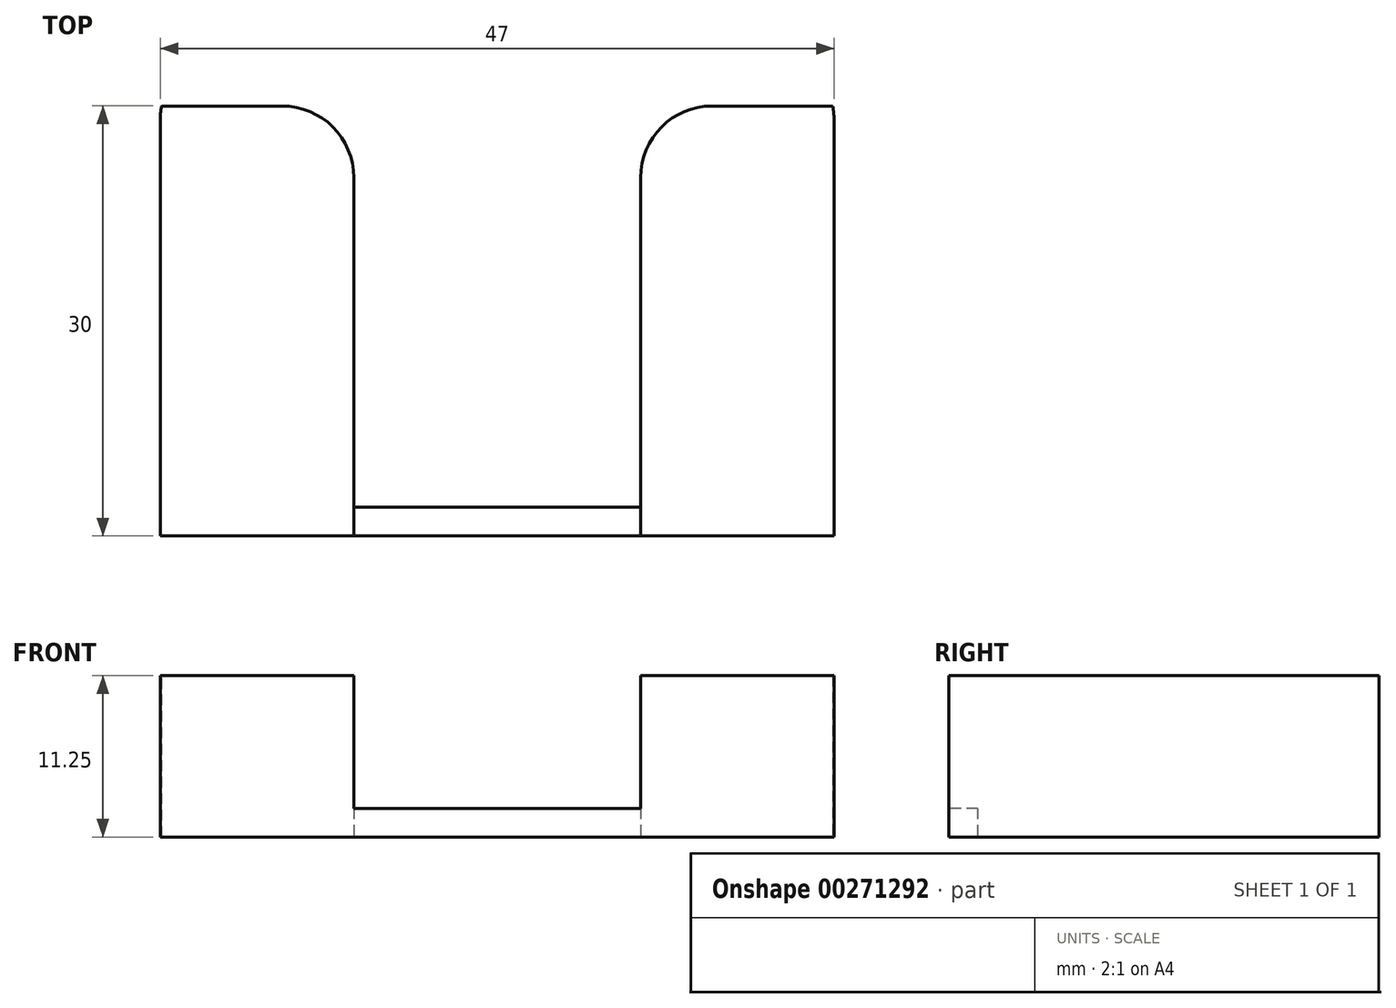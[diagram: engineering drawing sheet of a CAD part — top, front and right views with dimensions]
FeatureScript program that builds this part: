
annotation { "Feature Type Name" : "Feature", "Feature Type Description" : "" }
export const myFeature = defineFeature(function(context is Context, id is Id, definition is map)
    precondition{}
    {
        {
            var Q0;
            Q0=qCreatedBy(makeId("Top.planeOp"),FACE);
            var sketch = newSketch(context, id + "F0", { "sketchPlane" : qUnion([Q0])});
            skLineSegment(sketch, "E0.bottom", {"start": v(-22.69, 4.66) * mm, "end": v(24.31, 4.66) * mm});
            skLineSegment(sketch, "E0.top", {"start": v(-22.69, 0.66) * mm, "end": v(24.31, 0.66) * mm});
            skLineSegment(sketch, "E0.left", {"start": v(-22.69, 4.66) * mm, "end": v(-22.69, 0.66) * mm});
            skLineSegment(sketch, "E0.right", {"start": v(24.31, 4.66) * mm, "end": v(24.31, 0.66) * mm});
            skLineSegment(sketch, "E1.bottom", {"start": v(-22.69, 0.66) * mm, "end": v(-9.19, 0.66) * mm});
            skLineSegment(sketch, "E1.top", {"start": v(-22.69, -29.34) * mm, "end": v(-9.19, -29.34) * mm});
            skLineSegment(sketch, "E1.left", {"start": v(-22.69, 0.66) * mm, "end": v(-22.69, -29.34) * mm});
            skLineSegment(sketch, "E1.right", {"start": v(-9.19, 0.66) * mm, "end": v(-9.19, -29.34) * mm});
            skLineSegment(sketch, "E2.bottom", {"start": v(24.31, 0.66) * mm, "end": v(10.81, 0.66) * mm});
            skLineSegment(sketch, "E2.top", {"start": v(24.31, -29.34) * mm, "end": v(10.81, -29.34) * mm});
            skLineSegment(sketch, "E2.left", {"start": v(24.31, 0.66) * mm, "end": v(24.31, -29.34) * mm});
            skLineSegment(sketch, "E2.right", {"start": v(10.81, 0.66) * mm, "end": v(10.81, -29.34) * mm});
            skLineSegment(sketch, "E3.bottom", {"start": v(-5.64, -5.4) * mm, "end": v(7.26, -5.4) * mm});
            skLineSegment(sketch, "E3.top", {"start": v(-5.64, -25.3) * mm, "end": v(7.26, -25.3) * mm});
            skLineSegment(sketch, "E3.left", {"start": v(-5.64, -5.4) * mm, "end": v(-5.64, -25.3) * mm});
            skLineSegment(sketch, "E3.right", {"start": v(7.26, -5.4) * mm, "end": v(7.26, -25.3) * mm});
            skLineSegment(sketch, "E4.bottom", {"start": v(-9.19, -29.34) * mm, "end": v(10.81, -29.34) * mm});
            skLineSegment(sketch, "E4.top", {"start": v(-9.19, -27.34) * mm, "end": v(10.81, -27.34) * mm});
            skLineSegment(sketch, "E4.left", {"start": v(-9.19, -29.34) * mm, "end": v(-9.19, -27.34) * mm});
            skLineSegment(sketch, "E4.right", {"start": v(10.81, -29.34) * mm, "end": v(10.81, -27.34) * mm});
            skLineSegment(sketch, "E5.bottom", {"start": v(-7.69, 18.66) * mm, "end": v(7.31, 18.66) * mm});
            skLineSegment(sketch, "E5.top", {"start": v(-7.69, 4.66) * mm, "end": v(7.31, 4.66) * mm});
            skLineSegment(sketch, "E5.left", {"start": v(-7.69, 18.66) * mm, "end": v(-7.69, 4.66) * mm});
            skLineSegment(sketch, "E5.right", {"start": v(7.31, 18.66) * mm, "end": v(7.31, 4.66) * mm});
            skCircle(sketch, "E6", {"center": v(-0.19, 11.66) * mm, "radius": 3 * mm});
            skPoint(sketch, "E6.centerSnap0", {"position": v(-0.19, 18.66) * mm});
            skPoint(sketch, "E6.centerSnap1", {"position": v(-7.69, 11.66) * mm});
            skSolve(sketch);
        }
        {
            var Q0;
            Q0=makeQuery(id+"F0.imprint","IMPRINT",FACE,{"disambiguationData":[TD([[makeQuery(id+"F0.imprint","IMPRINT",EDGE,{"derivedFrom":sQuery(id+"F0.wireOp",EDGE,"E5.bottom")}),-1.0]])]});
            var Q1;
            Q1=makeQuery(id+"F0.imprint","IMPRINT",FACE,{"disambiguationData":[TD([[makeQuery(id+"F0.imprint","IMPRINT",EDGE,{"derivedFrom":sQuery(id+"F0.wireOp",EDGE,"E0.top")}),1.0]])]});
            var Q2;
            Q2=makeQuery(id+"F0.imprint","IMPRINT",FACE,{"disambiguationData":[TD([[makeQuery(id+"F0.imprint","IMPRINT",EDGE,{"derivedFrom":sQuery(id+"F0.wireOp",EDGE,"E1.bottom")}),-1.0]])]});
            var Q3;
            Q3=makeQuery(id+"F0.imprint","IMPRINT",FACE,{"disambiguationData":[TD([[makeQuery(id+"F0.imprint","IMPRINT",EDGE,{"derivedFrom":sQuery(id+"F0.wireOp",EDGE,"E2.bottom")}),1.0]])]});
            var Q4;
            Q4=makeQuery(id+"F0.imprint","IMPRINT",FACE,{"disambiguationData":[TD([[makeQuery(id+"F0.imprint","IMPRINT",EDGE,{"derivedFrom":sQuery(id+"F0.wireOp",EDGE,"E4.bottom")}),1.0]])]});
            extrude(context, id + "F1", {"entities" : qUnion([Q0, Q1, Q2, Q3, Q4]), "depth" : 2 * mm});
        }
        {
            var Q0;
            Q0=makeQuery(id+"F0.imprint","IMPRINT",FACE,{"disambiguationData":[TD([[makeQuery(id+"F0.imprint","IMPRINT",EDGE,{"derivedFrom":sQuery(id+"F0.wireOp",EDGE,"E0.top")}),-1.0]])]});
            extrude(context, id + "F2", {"entities" : qUnion([Q0]), "operationType" : NewBodyOperationType.ADD, "depth" : 11.25 * mm});
        }
        {
            var Q0;
            Q0=makeQuery(id+"F2.opExtrude","SWEPT_EDGE",EDGE,{"disambiguationData":[OSD([sQuery(id+"F0.wireOp",EDGE,"E0.top"),sQuery(id+"F0.wireOp",EDGE,"E2.bottom"),sQuery(id+"F0.wireOp",EDGE,"E2.right")])]});
            var Q1;
            Q1=makeQuery(id+"F2.opExtrude","SWEPT_EDGE",EDGE,{"disambiguationData":[OSD([sQuery(id+"F0.wireOp",EDGE,"E0.top"),sQuery(id+"F0.wireOp",EDGE,"E1.bottom"),sQuery(id+"F0.wireOp",EDGE,"E1.right")])]});
            var Q2;
            Q2=makeQuery(id+"F2.opExtrude","SWEPT_EDGE",EDGE,{"disambiguationData":[OSD([sQuery(id+"F0.wireOp",EDGE,"E1.right"),sQuery(id+"F0.wireOp",EDGE,"E4.top"),sQuery(id+"F0.wireOp",EDGE,"E4.left")])]});
            var Q3;
            Q3=makeQuery(id+"F2.opExtrude","SWEPT_EDGE",EDGE,{"disambiguationData":[OSD([sQuery(id+"F0.wireOp",EDGE,"E2.right"),sQuery(id+"F0.wireOp",EDGE,"E4.top"),sQuery(id+"F0.wireOp",EDGE,"E4.right")])]});
            var Q4;
            Q4=makeQuery(id+"F1.opExtrude","SWEPT_EDGE",EDGE,{"disambiguationData":[OSD([sQuery(id+"F0.wireOp",EDGE,"E2.top"),sQuery(id+"F0.wireOp",EDGE,"E2.left")])]});
            var Q5;
            Q5=makeQuery(id+"F1.opExtrude","SWEPT_EDGE",EDGE,{"disambiguationData":[OSD([sQuery(id+"F0.wireOp",EDGE,"E1.top"),sQuery(id+"F0.wireOp",EDGE,"E1.left")])]});
            var Q6;
            Q6=makeQuery(id+"F1.opExtrude","SWEPT_EDGE",EDGE,{"disambiguationData":[OSD([sQuery(id+"F0.wireOp",EDGE,"E0.bottom"),sQuery(id+"F0.wireOp",EDGE,"E0.right")])]});
            var Q7;
            Q7=makeQuery(id+"F1.opExtrude","SWEPT_EDGE",EDGE,{"disambiguationData":[OSD([sQuery(id+"F0.wireOp",EDGE,"E5.bottom"),sQuery(id+"F0.wireOp",EDGE,"E5.right")])]});
            var Q8;
            Q8=makeQuery(id+"F1.opExtrude","SWEPT_EDGE",EDGE,{"disambiguationData":[OSD([sQuery(id+"F0.wireOp",EDGE,"E5.bottom"),sQuery(id+"F0.wireOp",EDGE,"E5.left")])]});
            var Q9;
            Q9=makeQuery(id+"F1.opExtrude","SWEPT_EDGE",EDGE,{"disambiguationData":[OSD([sQuery(id+"F0.wireOp",EDGE,"E0.bottom"),sQuery(id+"F0.wireOp",EDGE,"E0.left")])]});
            var Q10;
            Q10=makeQuery(id+"F1.opExtrude","SWEPT_EDGE",EDGE,{"disambiguationData":[OSD([sQuery(id+"F0.wireOp",EDGE,"E0.bottom"),sQuery(id+"F0.wireOp",EDGE,"E5.top"),sQuery(id+"F0.wireOp",EDGE,"E5.left")])]});
            var Q11;
            Q11=makeQuery(id+"F1.opExtrude","SWEPT_EDGE",EDGE,{"disambiguationData":[OSD([sQuery(id+"F0.wireOp",EDGE,"E0.bottom"),sQuery(id+"F0.wireOp",EDGE,"E5.top"),sQuery(id+"F0.wireOp",EDGE,"E5.right")])]});
            fillet(context, id + "F3", {"entities" : qUnion([Q0, Q1, Q2, Q3, Q4, Q5, Q6, Q7, Q8, Q9, Q10, Q11]), "radius" : 5 * mm, "tangentPropagation" : true, "allowEdgeOverflow" : false});
        }
        {
            var Q0;
            {var subQ0=sQuery(id+"F0.wireOp",EDGE,"E4.top");var subQ1=sQuery(id+"F0.wireOp",EDGE,"E2.right");var subQ2=sQuery(id+"F0.wireOp",EDGE,"E1.right");var subQ3=sQuery(id+"F0.wireOp",EDGE,"E0.top");Q0=makeQuery(id+"F2.boolean.opBoolean","MERGE",FACE,{"derivedFrom":[makeQuery(id+"F1.opExtrude","CAP_FACE",FACE,{"disambiguationData":[OSD([sQuery(id+"F0.wireOp",EDGE,"E0.bottom"),subQ3,sQuery(id+"F0.wireOp",EDGE,"E0.left"),sQuery(id+"F0.wireOp",EDGE,"E0.right"),sQuery(id+"F0.wireOp",EDGE,"E1.top"),sQuery(id+"F0.wireOp",EDGE,"E1.left"),subQ2,sQuery(id+"F0.wireOp",EDGE,"E2.top"),sQuery(id+"F0.wireOp",EDGE,"E2.left"),subQ1,sQuery(id+"F0.wireOp",EDGE,"e83457b0-2eee-4cfc-8b23-16ca087f3800"),sQuery(id+"F0.wireOp",EDGE,"f83d8425-d4e3-404a-83f3-46c32a1b02bb"),sQuery(id+"F0.wireOp",EDGE,"E4.bottom"),subQ0,sQuery(id+"F0.wireOp",EDGE,"E5.bottom"),sQuery(id+"F0.wireOp",EDGE,"E5.left"),sQuery(id+"F0.wireOp",EDGE,"E5.right"),sQuery(id+"F0.wireOp",EDGE,"E6")])],"isStart":true}),makeQuery(id+"F2.opExtrude","CAP_FACE",FACE,{"disambiguationData":[OSD([subQ3,subQ2,subQ1,sQuery(id+"F0.wireOp",EDGE,"E3.bottom"),sQuery(id+"F0.wireOp",EDGE,"E3.top"),sQuery(id+"F0.wireOp",EDGE,"E3.left"),sQuery(id+"F0.wireOp",EDGE,"E3.right"),subQ0])],"isStart":true})]});}
            var sketch = newSketch(context, id + "F4", { "sketchPlane" : qUnion([Q0])});
            skLineSegment(sketch, "E7.bottom", {"start": v(-0.14, 25.3) * mm, "end": v(1.86, 25.3) * mm});
            skLineSegment(sketch, "E7.top", {"start": v(-0.14, 26.3) * mm, "end": v(1.86, 26.3) * mm});
            skLineSegment(sketch, "E7.left", {"start": v(-0.14, 25.3) * mm, "end": v(-0.14, 26.3) * mm});
            skLineSegment(sketch, "E7.right", {"start": v(1.86, 25.3) * mm, "end": v(1.86, 26.3) * mm});
            skLineSegment(sketch, "E8.bottom", {"start": v(-0.14, 5.4) * mm, "end": v(1.86, 5.4) * mm});
            skLineSegment(sketch, "E8.top", {"start": v(-0.14, 4.4) * mm, "end": v(1.86, 4.4) * mm});
            skLineSegment(sketch, "E8.left", {"start": v(-0.14, 5.4) * mm, "end": v(-0.14, 4.4) * mm});
            skLineSegment(sketch, "E8.right", {"start": v(1.86, 5.4) * mm, "end": v(1.86, 4.4) * mm});
            skSolve(sketch);
        }
        {
            var Q0;
            Q0=makeQuery(id+"F4.imprint","IMPRINT",FACE,{"disambiguationData":[TD([[makeQuery(id+"F4.imprint","IMPRINT",EDGE,{"derivedFrom":sQuery(id+"F4.wireOp",EDGE,"E7.bottom")}),1.0]])]});
            var Q1;
            Q1=makeQuery(id+"F4.imprint","IMPRINT",FACE,{"disambiguationData":[TD([[makeQuery(id+"F4.imprint","IMPRINT",EDGE,{"derivedFrom":sQuery(id+"F4.wireOp",EDGE,"E8.bottom")}),-1.0]])]});
            extrude(context, id + "F5", {"entities" : qUnion([Q0, Q1]), "operationType" : NewBodyOperationType.REMOVE, "oppositeDirection" : true, "depth" : 2 * mm});
        }
        {
            var Q0;
            Q0=makeQuery(id+"F1.opExtrude","CAP_FACE",FACE,{"disambiguationData":[OSD([sQuery(id+"F0.wireOp",EDGE,"E0.bottom"),sQuery(id+"F0.wireOp",EDGE,"E0.top"),sQuery(id+"F0.wireOp",EDGE,"E0.left"),sQuery(id+"F0.wireOp",EDGE,"E0.right"),sQuery(id+"F0.wireOp",EDGE,"E1.top"),sQuery(id+"F0.wireOp",EDGE,"E1.left"),sQuery(id+"F0.wireOp",EDGE,"E1.right"),sQuery(id+"F0.wireOp",EDGE,"E2.top"),sQuery(id+"F0.wireOp",EDGE,"E2.left"),sQuery(id+"F0.wireOp",EDGE,"E2.right"),sQuery(id+"F0.wireOp",EDGE,"E4.bottom"),sQuery(id+"F0.wireOp",EDGE,"E4.top"),sQuery(id+"F0.wireOp",EDGE,"E5.bottom"),sQuery(id+"F0.wireOp",EDGE,"E5.left"),sQuery(id+"F0.wireOp",EDGE,"E5.right"),sQuery(id+"F0.wireOp",EDGE,"E6")])],"isStart":false});
            var sketch = newSketch(context, id + "F6", { "sketchPlane" : qUnion([Q0])});
            skCircle(sketch, "E9", {"center": v(-15.69, -23.34) * mm, "radius": 2.75 * mm});
            skCircle(sketch, "E10", {"center": v(17.31, -23.34) * mm, "radius": 2.75 * mm});
            skCircle(sketch, "E11", {"center": v(-15.69, -23.34) * mm, "radius": 4.5 * mm});
            skCircle(sketch, "E12", {"center": v(17.31, -23.34) * mm, "radius": 4.5 * mm});
            skCircle(sketch, "E13", {"center": v(-0.19, 11.66) * mm, "radius": 1.8 * mm});
            skSolve(sketch);
        }
        {
            var Q0;
            Q0=makeQuery(id+"F6.imprint","IMPRINT",FACE,{"disambiguationData":[TD([[makeQuery(id+"F6.imprint","IMPRINT",EDGE,{"derivedFrom":sQuery(id+"F6.wireOp",EDGE,"E9")}),-1.0]])]});
            var Q1;
            Q1=makeQuery(id+"F6.imprint","IMPRINT",FACE,{"disambiguationData":[TD([[makeQuery(id+"F6.imprint","IMPRINT",EDGE,{"derivedFrom":sQuery(id+"F6.wireOp",EDGE,"E10")}),-1.0]])]});
            extrude(context, id + "F7", {"entities" : qUnion([Q0, Q1]), "operationType" : NewBodyOperationType.ADD, "depth" : 9.25 * mm});
        }
        {
            var Q0;
            Q0=makeQuery(id+"F7.boolean.opBoolean","SPLIT",FACE,{"disambiguationData":[TD([makeQuery(id+"F7.opExtrude","SWEPT_FACE",FACE,{"disambiguationData":[OSD([sQuery(id+"F6.wireOp",EDGE,"E9")])]})])],"derivedFrom":makeQuery(id+"F1.opExtrude","CAP_FACE",FACE,{"disambiguationData":[OSD([sQuery(id+"F0.wireOp",EDGE,"E0.bottom"),sQuery(id+"F0.wireOp",EDGE,"E0.top"),sQuery(id+"F0.wireOp",EDGE,"E0.left"),sQuery(id+"F0.wireOp",EDGE,"E0.right"),sQuery(id+"F0.wireOp",EDGE,"E1.top"),sQuery(id+"F0.wireOp",EDGE,"E1.left"),sQuery(id+"F0.wireOp",EDGE,"E1.right"),sQuery(id+"F0.wireOp",EDGE,"E2.top"),sQuery(id+"F0.wireOp",EDGE,"E2.left"),sQuery(id+"F0.wireOp",EDGE,"E2.right"),sQuery(id+"F0.wireOp",EDGE,"E4.bottom"),sQuery(id+"F0.wireOp",EDGE,"E4.top"),sQuery(id+"F0.wireOp",EDGE,"E5.bottom"),sQuery(id+"F0.wireOp",EDGE,"E5.left"),sQuery(id+"F0.wireOp",EDGE,"E5.right"),sQuery(id+"F0.wireOp",EDGE,"E6")])],"isStart":false})});
            var Q1;
            Q1=makeQuery(id+"F7.boolean.opBoolean","SPLIT",FACE,{"disambiguationData":[TD([makeQuery(id+"F7.opExtrude","SWEPT_FACE",FACE,{"disambiguationData":[OSD([sQuery(id+"F6.wireOp",EDGE,"E10")])]})])],"derivedFrom":makeQuery(id+"F1.opExtrude","CAP_FACE",FACE,{"disambiguationData":[OSD([sQuery(id+"F0.wireOp",EDGE,"E0.bottom"),sQuery(id+"F0.wireOp",EDGE,"E0.top"),sQuery(id+"F0.wireOp",EDGE,"E0.left"),sQuery(id+"F0.wireOp",EDGE,"E0.right"),sQuery(id+"F0.wireOp",EDGE,"E1.top"),sQuery(id+"F0.wireOp",EDGE,"E1.left"),sQuery(id+"F0.wireOp",EDGE,"E1.right"),sQuery(id+"F0.wireOp",EDGE,"E2.top"),sQuery(id+"F0.wireOp",EDGE,"E2.left"),sQuery(id+"F0.wireOp",EDGE,"E2.right"),sQuery(id+"F0.wireOp",EDGE,"E4.bottom"),sQuery(id+"F0.wireOp",EDGE,"E4.top"),sQuery(id+"F0.wireOp",EDGE,"E5.bottom"),sQuery(id+"F0.wireOp",EDGE,"E5.left"),sQuery(id+"F0.wireOp",EDGE,"E5.right"),sQuery(id+"F0.wireOp",EDGE,"E6")])],"isStart":false})});
            extrude(context, id + "F8", {"entities" : qUnion([Q0, Q1]), "operationType" : NewBodyOperationType.REMOVE, "endBound" : BoundingType.THROUGH_ALL, "oppositeDirection" : true, "depth" : 25 * mm});
        }
    });
